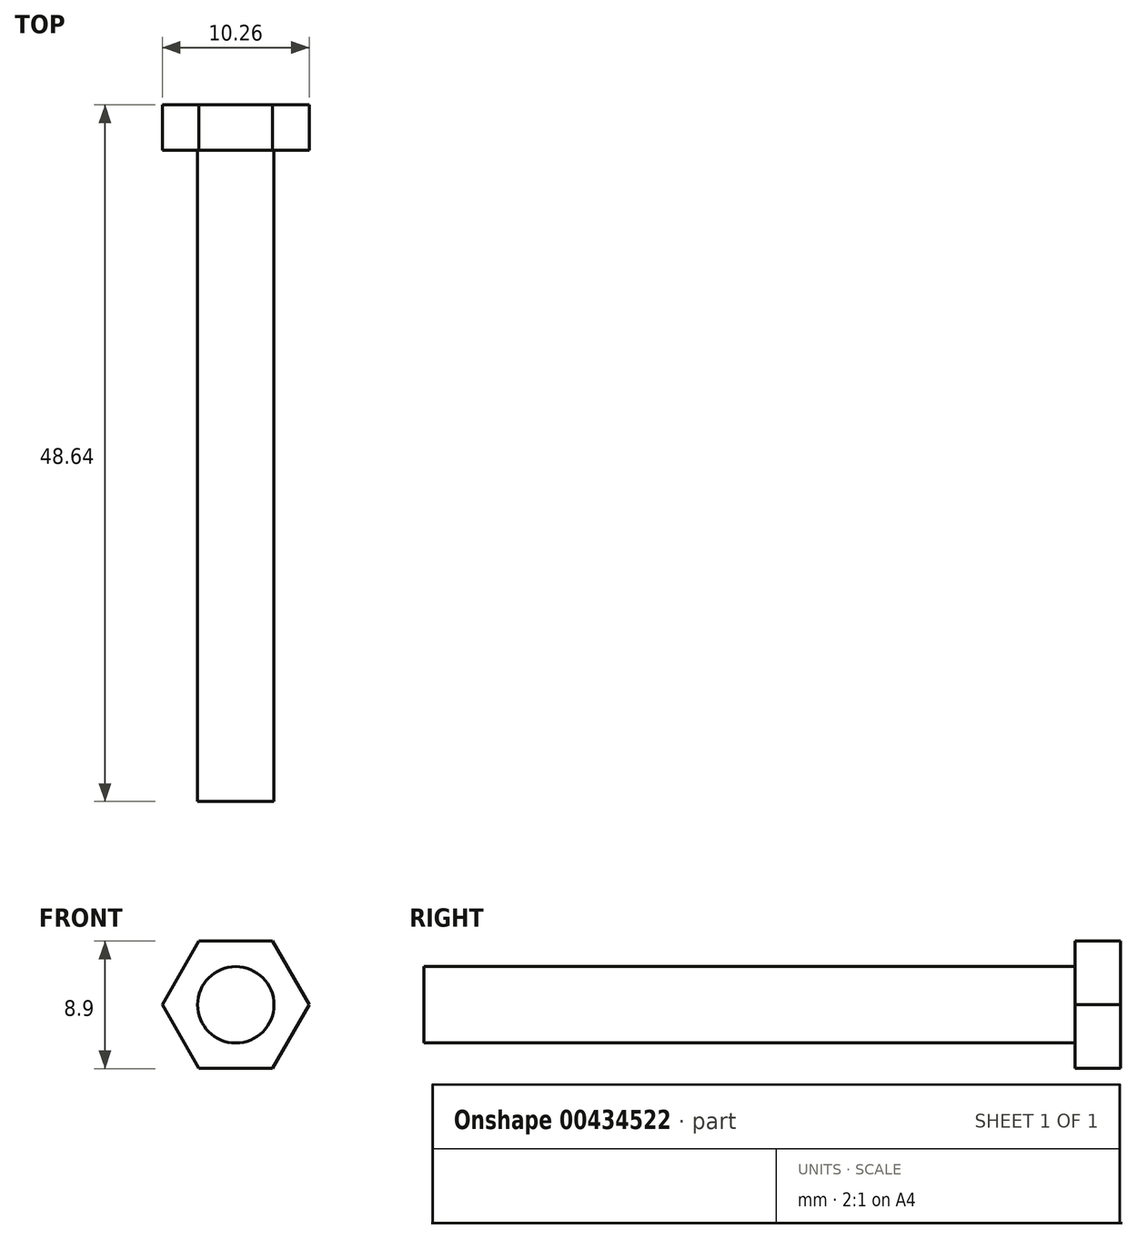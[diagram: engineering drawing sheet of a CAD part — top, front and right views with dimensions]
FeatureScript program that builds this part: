
annotation { "Feature Type Name" : "Feature", "Feature Type Description" : "" }
export const myFeature = defineFeature(function(context is Context, id is Id, definition is map)
    precondition{}
    {
        {
            var Q0;
            Q0=qCreatedBy(makeId("Front.planeOp"),FACE);
            var sketch = newSketch(context, id + "F0", { "sketchPlane" : qUnion([Q0])});
            skCircle(sketch, "E0.cCircle", {"center": v(0, 0) * mm, "radius": 4.44 * mm, "construction": true});
            skLineSegment(sketch, "E0.0", {"start": v(-2.57, 4.44) * mm, "end": v(2.57, 4.44) * mm});
            skLineSegment(sketch, "E0.1", {"start": v(2.57, 4.44) * mm, "end": v(5.13, 0) * mm});
            skLineSegment(sketch, "E0.2", {"start": v(5.13, 0) * mm, "end": v(2.57, -4.44) * mm});
            skLineSegment(sketch, "E0.3", {"start": v(2.57, -4.44) * mm, "end": v(-2.57, -4.45) * mm});
            skLineSegment(sketch, "E0.4", {"start": v(-2.57, -4.45) * mm, "end": v(-5.13, 0) * mm});
            skLineSegment(sketch, "E0.5", {"start": v(-5.13, 0) * mm, "end": v(-2.57, 4.44) * mm});
            skPoint(sketch, "E0.0.midPoint", {"position": v(0, 4.44) * mm});
            skCircle(sketch, "E1", {"center": v(0, 0) * mm, "radius": 2.67 * mm});
            skSolve(sketch);
        }
        {
            var Q0;
            Q0 = qSketchRegion(id + "F0", true);
            var Q1;
            Q1=makeQuery(id+"F0.imprint","IMPRINT",FACE,{"disambiguationData":[TD([[makeQuery(id+"F0.imprint","IMPRINT",EDGE,{"derivedFrom":sQuery(id+"F0.wireOp",EDGE,"E1")}),1.0]])]});
            extrude(context, id + "F1", {"entities" : qUnion([Q0, Q1]), "depth" : 3.17 * mm});
        }
        {
            var Q0;
            Q0=makeQuery(id+"F0.imprint","IMPRINT",FACE,{"disambiguationData":[TD([[makeQuery(id+"F0.imprint","IMPRINT",EDGE,{"derivedFrom":sQuery(id+"F0.wireOp",EDGE,"E1")}),1.0]])]});
            extrude(context, id + "F2", {"entities" : qUnion([Q0]), "operationType" : NewBodyOperationType.ADD, "depth" : 48.64 * mm});
        }
    });
